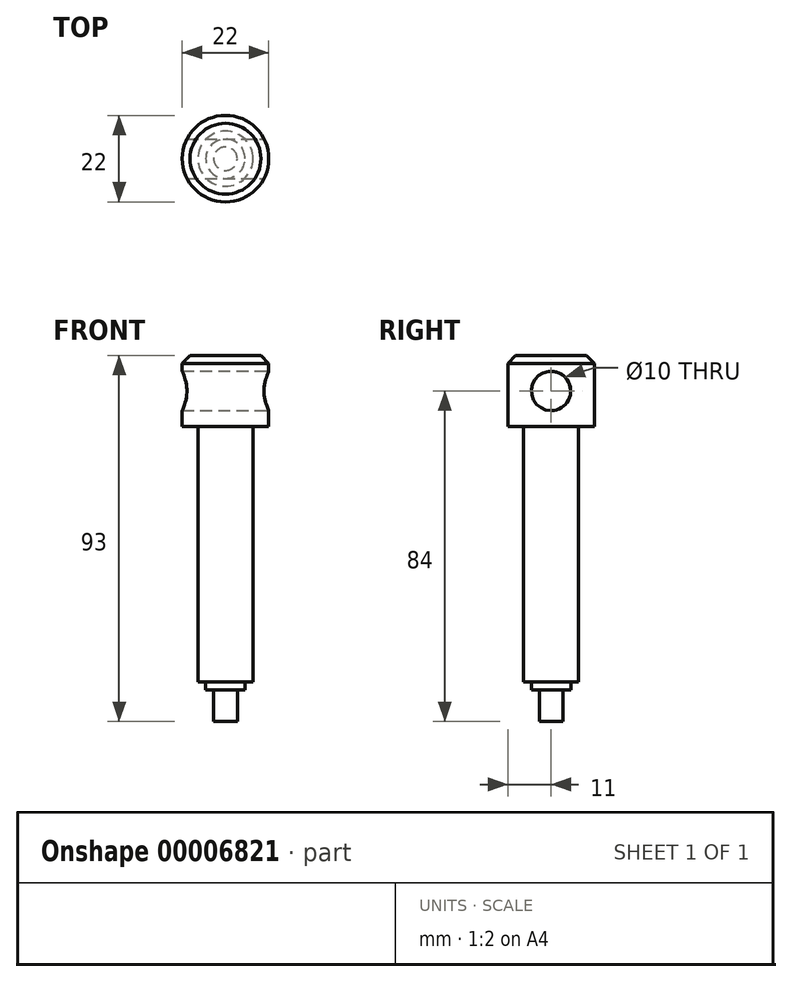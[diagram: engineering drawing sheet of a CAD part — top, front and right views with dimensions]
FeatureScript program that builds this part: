
annotation { "Feature Type Name" : "Feature", "Feature Type Description" : "" }
export const myFeature = defineFeature(function(context is Context, id is Id, definition is map)
    precondition{}
    {
        {
            var Q0;
            Q0=qCreatedBy(makeId("Right.planeOp"),FACE);
            var sketch = newSketch(context, id + "F0", { "sketchPlane" : qUnion([Q0])});
            skLineSegment(sketch, "E0", {"start": v(0, 0) * mm, "end": v(0, -3.09) * mm});
            skLineSegment(sketch, "E1", {"start": v(4.26, -9.53) * mm, "end": v(36, -23) * mm});
            skLineSegment(sketch, "E2", {"start": v(36, -23) * mm, "end": v(70, -23) * mm});
            skLineSegment(sketch, "E3", {"start": v(90, -3) * mm, "end": v(90, 47) * mm});
            skLineSegment(sketch, "E4", {"start": v(70, 67) * mm, "end": v(7, 67) * mm});
            skLineSegment(sketch, "E5", {"start": v(7, 67) * mm, "end": v(7, 45) * mm});
            skLineSegment(sketch, "E6", {"start": v(7, 45) * mm, "end": v(61, 45) * mm});
            skLineSegment(sketch, "E7", {"start": v(68, 38) * mm, "end": v(68, 4) * mm});
            skLineSegment(sketch, "E8", {"start": v(61, -3) * mm, "end": v(36, -3) * mm});
            skLineSegment(sketch, "E9", {"start": v(36, -3) * mm, "end": v(36, 0) * mm});
            skLineSegment(sketch, "E10", {"start": v(36, 0) * mm, "end": v(0, 0) * mm});
            skLineSegment(sketch, "E11", {"start": v(36, -23) * mm, "end": v(21.85, -23) * mm, "construction": true});
            skPoint(sketch, "E12.visualSharp", {"position": v(90, -23) * mm});
            skArc(sketch, "E12.filletArc", {"start": v(70, -23) * mm, "mid": v(84.14, -17.14) * mm, "end": v(90, -3) * mm});
            skPoint(sketch, "E13.visualSharp", {"position": v(90, 67) * mm});
            skArc(sketch, "E13.filletArc", {"start": v(90, 47) * mm, "mid": v(84.14, 61.14) * mm, "end": v(70, 67) * mm});
            skPoint(sketch, "E14.visualSharp", {"position": v(68, 45) * mm});
            skArc(sketch, "E14.filletArc", {"start": v(68, 38) * mm, "mid": v(65.95, 42.95) * mm, "end": v(61, 45) * mm});
            skPoint(sketch, "E15.visualSharp", {"position": v(68, -3) * mm});
            skArc(sketch, "E15.filletArc", {"start": v(61, -3) * mm, "mid": v(65.95, -0.95) * mm, "end": v(68, 4) * mm});
            skPoint(sketch, "E16.visualSharp", {"position": v(0, -7.72) * mm});
            skArc(sketch, "E16.filletArc", {"start": v(0, -3.09) * mm, "mid": v(1.16, -6.95) * mm, "end": v(4.26, -9.53) * mm});
            skSolve(sketch);
        }
        {
            var Q0;
            Q0=qSketchRegion(id+"F0",true);
            extrude(context, id + "F1", {"entities" : qUnion([Q0]), "endBound" : BoundingType.SYMMETRIC, "depth" : 20 * mm});
        }
        {
            var Q0;
            Q0=makeQuery(id+"F1.opExtrude","SWEPT_FACE",FACE,{"disambiguationData":[OSD([sQuery(id+"F0.wireOp",EDGE,"E6")])]});
            var sketch = newSketch(context, id + "F2", { "sketchPlane" : qUnion([Q0])});
            skCircle(sketch, "E17", {"center": v(0, -18) * mm, "radius": 11 * mm});
            skCircle(sketch, "E18", {"center": v(0, -18) * mm, "radius": 7 * mm});
            skSolve(sketch);
        }
        {
            var Q0;
            Q0=qSketchRegion(id+"F2",true);
            extrude(context, id + "F3", {"entities" : qUnion([Q0]), "operationType" : NewBodyOperationType.ADD, "oppositeDirection" : true, "depth" : 25 * mm});
        }
        {
            var Q0;
            Q0=makeQuery(id+"F3.boolean.opBoolean","SPLIT",FACE,{"disambiguationData":[TD([makeQuery(id+"F3.opExtrude","SWEPT_FACE",FACE,{"disambiguationData":[OSD([sQuery(id+"F2.wireOp",EDGE,"E18")])]})])],"derivedFrom":makeQuery(id+"F1.opExtrude","SWEPT_FACE",FACE,{"disambiguationData":[OSD([sQuery(id+"F0.wireOp",EDGE,"E4")])]})});
            var sketch = newSketch(context, id + "F4", { "sketchPlane" : qUnion([Q0])});
            skCircle(sketch, "E19.0", {"center": v(0, 18) * mm, "radius": 7 * mm});
            skSolve(sketch);
        }
        {
            var Q0;
            Q0=qSketchRegion(id+"F4",true);
            extrude(context, id + "F5", {"entities" : qUnion([Q0]), "operationType" : NewBodyOperationType.REMOVE, "oppositeDirection" : true, "depth" : 25 * mm});
        }
        {
            var Q0;
            {var subQ0=sQuery(id+"F0.wireOp",EDGE,"E4");var subQ1=makeQuery(id+"F1.opExtrude","SWEPT_FACE",FACE,{"disambiguationData":[OSD([subQ0])]});var subQ2=sQuery(id+"F0.wireOp",EDGE,"E5");Q0=makeQuery(id+"F3.boolean.opBoolean","SPLIT",FACE,{"disambiguationData":[TD([makeQuery(id+"F1.opExtrude","CAP_FACE",FACE,{"disambiguationData":[OSD([sQuery(id+"F0.wireOp",EDGE,"E0"),sQuery(id+"F0.wireOp",EDGE,"E1"),sQuery(id+"F0.wireOp",EDGE,"E2"),sQuery(id+"F0.wireOp",EDGE,"E3"),subQ0,subQ2,sQuery(id+"F0.wireOp",EDGE,"E6"),sQuery(id+"F0.wireOp",EDGE,"E7"),sQuery(id+"F0.wireOp",EDGE,"E8"),sQuery(id+"F0.wireOp",EDGE,"E9"),sQuery(id+"F0.wireOp",EDGE,"E10"),sQuery(id+"F0.wireOp",EDGE,"E12.filletArc"),sQuery(id+"F0.wireOp",EDGE,"E13.filletArc"),sQuery(id+"F0.wireOp",EDGE,"E14.filletArc"),sQuery(id+"F0.wireOp",EDGE,"E15.filletArc"),sQuery(id+"F0.wireOp",EDGE,"E16.filletArc")])],"isStart":false}),subQ1,makeQuery(id+"F1.opExtrude","SWEPT_FACE",FACE,{"disambiguationData":[OSD([subQ2])]}),makeQuery(id+"F3.opExtrude","SWEPT_FACE",FACE,{"disambiguationData":[OSD([sQuery(id+"F2.wireOp",EDGE,"E17")])]})])],"derivedFrom":subQ1});}
            var sketch = newSketch(context, id + "F6", { "sketchPlane" : qUnion([Q0])});
            skLineSegment(sketch, "E20.1.0", {"start": v(-10, 7) * mm, "end": v(0, 7) * mm});
            skArc(sketch, "E20.1.1", {"start": v(0, 7) * mm, "mid": v(-5.94, 8.74) * mm, "end": v(-10, 13.42) * mm});
            skLineSegment(sketch, "E20.1.2", {"start": v(-10, 13.42) * mm, "end": v(-10, 7) * mm});
            skSolve(sketch);
        }
        {
            var Q0;
            Q0=qSketchRegion(id+"F6",true);
            extrude(context, id + "F7", {"entities" : qUnion([Q0]), "operationType" : NewBodyOperationType.REMOVE, "oppositeDirection" : true, "depth" : 25 * mm});
        }
        {
            var Q0;
            {var subQ0=sQuery(id+"F0.wireOp",EDGE,"E4");var subQ1=makeQuery(id+"F1.opExtrude","SWEPT_FACE",FACE,{"disambiguationData":[OSD([subQ0])]});var subQ2=sQuery(id+"F0.wireOp",EDGE,"E5");Q0=makeQuery(id+"F3.boolean.opBoolean","SPLIT",FACE,{"disambiguationData":[TD([makeQuery(id+"F1.opExtrude","CAP_FACE",FACE,{"disambiguationData":[OSD([sQuery(id+"F0.wireOp",EDGE,"E0"),sQuery(id+"F0.wireOp",EDGE,"E1"),sQuery(id+"F0.wireOp",EDGE,"E2"),sQuery(id+"F0.wireOp",EDGE,"E3"),subQ0,subQ2,sQuery(id+"F0.wireOp",EDGE,"E6"),sQuery(id+"F0.wireOp",EDGE,"E7"),sQuery(id+"F0.wireOp",EDGE,"E8"),sQuery(id+"F0.wireOp",EDGE,"E9"),sQuery(id+"F0.wireOp",EDGE,"E10"),sQuery(id+"F0.wireOp",EDGE,"E12.filletArc"),sQuery(id+"F0.wireOp",EDGE,"E13.filletArc"),sQuery(id+"F0.wireOp",EDGE,"E14.filletArc"),sQuery(id+"F0.wireOp",EDGE,"E15.filletArc"),sQuery(id+"F0.wireOp",EDGE,"E16.filletArc")])],"isStart":false}),subQ1,makeQuery(id+"F1.opExtrude","SWEPT_FACE",FACE,{"disambiguationData":[OSD([subQ2])]}),makeQuery(id+"F3.opExtrude","SWEPT_FACE",FACE,{"disambiguationData":[OSD([sQuery(id+"F2.wireOp",EDGE,"E17")])]})])],"derivedFrom":subQ1});}
            var sketch = newSketch(context, id + "F8", { "sketchPlane" : qUnion([Q0])});
            skArc(sketch, "E21.0", {"start": v(10, 13.42) * mm, "mid": v(5.94, 8.74) * mm, "end": v(0, 7) * mm});
            skLineSegment(sketch, "E22", {"start": v(10, 13.42) * mm, "end": v(10, 7) * mm});
            skLineSegment(sketch, "E23", {"start": v(10, 7) * mm, "end": v(0, 7) * mm});
            skSolve(sketch);
        }
        {
            var Q0;
            Q0=qSketchRegion(id+"F8",true);
            extrude(context, id + "F9", {"entities" : qUnion([Q0]), "operationType" : NewBodyOperationType.REMOVE, "oppositeDirection" : true, "depth" : 25 * mm});
        }
        {
            var Q0;
            Q0=makeQuery(id+"F1.opExtrude","SWEPT_EDGE",EDGE,{"disambiguationData":[OSD([sQuery(id+"F0.wireOp",EDGE,"E8"),sQuery(id+"F0.wireOp",EDGE,"E9")])]});
            fillet(context, id + "F10", {"entities" : qUnion([Q0]), "radius" : 3 * mm, "tangentPropagation" : true, "allowEdgeOverflow" : false});
        }
        {
            var Q0;
            Q0=qCreatedBy(makeId("Right.planeOp"),FACE);
            var sketch = newSketch(context, id + "F11", { "sketchPlane" : qUnion([Q0])});
            skLineSegment(sketch, "E24", {"start": v(11, 100) * mm, "end": v(7, 100) * mm});
            skLineSegment(sketch, "E25", {"start": v(7, 100) * mm, "end": v(7, 118) * mm});
            skLineSegment(sketch, "E26", {"start": v(7, 118) * mm, "end": v(18, 118) * mm});
            skLineSegment(sketch, "E27", {"start": v(18, 118) * mm, "end": v(18, 35) * mm});
            skLineSegment(sketch, "E28", {"start": v(11, 100) * mm, "end": v(11, 35) * mm});
            skLineSegment(sketch, "E29", {"start": v(11, 35) * mm, "end": v(18, 35) * mm});
            skSolve(sketch);
        }
        {
            var Q0;
            Q0=qSketchRegion(id+"F11",true);
            var Q1;
            Q1=sQuery(id+"F11.wireOp",EDGE,"E27");
            revolve(context, id + "F12", {"entities" : qUnion([Q0]), "axis" : qUnion([Q1]), "revolveType" : RevolveType.FULL});
        }
        {
            var Q0;
            Q0=makeQuery(id+"F12.opRevolve","SWEPT_EDGE",EDGE,{"disambiguationData":[OSD([sQuery(id+"F11.wireOp",EDGE,"E25"),sQuery(id+"F11.wireOp",EDGE,"E26")])]});
            chamfer(context, id + "F13", {"entities" : qUnion([Q0]), "width" : 2 * mm, "tangentPropagation" : true});
        }
        {
            var Q0;
            Q0=makeQuery(id+"F12.opRevolve","SWEPT_FACE",FACE,{"disambiguationData":[OSD([sQuery(id+"F11.wireOp",EDGE,"E29")])]});
            var sketch = newSketch(context, id + "F14", { "sketchPlane" : qUnion([Q0])});
            skCircle(sketch, "E30", {"center": v(0, -18) * mm, "radius": 5 * mm});
            skSolve(sketch);
        }
        {
            var Q0;
            Q0=qSketchRegion(id+"F14",true);
            extrude(context, id + "F15", {"entities" : qUnion([Q0]), "operationType" : NewBodyOperationType.ADD, "depth" : 2 * mm});
        }
        {
            var Q0;
            Q0=makeQuery(id+"F15.opExtrude","CAP_FACE",FACE,{"disambiguationData":[OSD([sQuery(id+"F14.wireOp",EDGE,"E30")])],"isStart":false});
            var sketch = newSketch(context, id + "F16", { "sketchPlane" : qUnion([Q0])});
            skCircle(sketch, "E31", {"center": v(0, -18) * mm, "radius": 3 * mm});
            skSolve(sketch);
        }
        {
            var Q0;
            Q0=qSketchRegion(id+"F16",true);
            extrude(context, id + "F17", {"entities" : qUnion([Q0]), "operationType" : NewBodyOperationType.ADD, "depth" : 8 * mm});
        }
        {
            var Q0;
            Q0=qCreatedBy(makeId("Right.planeOp"),FACE);
            var sketch = newSketch(context, id + "F18", { "sketchPlane" : qUnion([Q0])});
            skCircle(sketch, "E32", {"center": v(18, 109) * mm, "radius": 5 * mm});
            skSolve(sketch);
        }
        {
            var Q0;
            Q0=qSketchRegion(id+"F18",true);
            extrude(context, id + "F19", {"entities" : qUnion([Q0]), "operationType" : NewBodyOperationType.REMOVE, "oppositeDirection" : true, "depth" : 25 * mm});
        }
        {
            var Q0;
            Q0=makeQuery(id+"F19.boolean.opBoolean","COPY",FACE,{"derivedFrom":makeQuery(id+"F19.opExtrude","CAP_FACE",FACE,{"disambiguationData":[OSD([sQuery(id+"F18.wireOp",EDGE,"E32")])],"isStart":true})});
            var sketch = newSketch(context, id + "F20", { "sketchPlane" : qUnion([Q0])});
            skCircle(sketch, "E33.0", {"center": v(-18, 109) * mm, "radius": 5 * mm});
            skSolve(sketch);
        }
        {
            var Q0;
            Q0=qSketchRegion(id+"F20",true);
            extrude(context, id + "F21", {"entities" : qUnion([Q0]), "operationType" : NewBodyOperationType.REMOVE, "oppositeDirection" : true, "depth" : 25 * mm});
        }
        {
            var Q0;
            Q0=qCreatedBy(makeId("Right.planeOp"),FACE);
            var sketch = newSketch(context, id + "F22", { "sketchPlane" : qUnion([Q0])});
            skCircle(sketch, "E34.0", {"center": v(18, 109) * mm, "radius": 5 * mm});
            skSolve(sketch);
        }
        {
            var Q0;
            Q0=qSketchRegion(id+"F22",true);
            extrude(context, id + "F23", {"entities" : qUnion([Q0]), "endBound" : BoundingType.SYMMETRIC, "depth" : 89 * mm});
        }
        {
            var Q0;
            Q0=makeQuery(id+"F23.opExtrude","CAP_FACE",FACE,{"disambiguationData":[OSD([sQuery(id+"F22.wireOp",EDGE,"E34.0")])],"isStart":false});
            var sketch = newSketch(context, id + "F24", { "sketchPlane" : qUnion([Q0])});
            skCircle(sketch, "E35", {"center": v(18, 109) * mm, "radius": 3 * mm});
            skSolve(sketch);
        }
        {
            var Q0;
            Q0=qSketchRegion(id+"F24",true);
            extrude(context, id + "F25", {"entities" : qUnion([Q0]), "operationType" : NewBodyOperationType.ADD, "depth" : 12 * mm});
        }
        {
            var Q0;
            Q0=makeQuery(id+"F23.opExtrude","CAP_FACE",FACE,{"disambiguationData":[OSD([sQuery(id+"F22.wireOp",EDGE,"E34.0")])],"isStart":true});
            var sketch = newSketch(context, id + "F26", { "sketchPlane" : qUnion([Q0])});
            skCircle(sketch, "E36", {"center": v(-18, 109) * mm, "radius": 3 * mm});
            skSolve(sketch);
        }
        {
            var Q0;
            Q0=qSketchRegion(id+"F26",true);
            extrude(context, id + "F27", {"entities" : qUnion([Q0]), "operationType" : NewBodyOperationType.ADD, "depth" : 12 * mm});
        }
        {
            var Q0;
            Q0=makeQuery(id+"F25.opExtrude","CAP_FACE",FACE,{"disambiguationData":[OSD([sQuery(id+"F24.wireOp",EDGE,"E35")])],"isStart":false});
            var sketch = newSketch(context, id + "F28", { "sketchPlane" : qUnion([Q0])});
            skCircle(sketch, "E37.0", {"center": v(18, 109) * mm, "radius": 3 * mm});
            skCircle(sketch, "E38", {"center": v(18, 109) * mm, "radius": 10 * mm});
            skSolve(sketch);
        }
        {
            var Q0;
            Q0=qSketchRegion(id+"F28",true);
            extrude(context, id + "F29", {"entities" : qUnion([Q0]), "oppositeDirection" : true, "depth" : 10 * mm});
        }
        {
            var Q0;
            Q0=makeQuery(id+"F29.opExtrude","CAP_EDGE",EDGE,{"disambiguationData":[OSD([sQuery(id+"F28.wireOp",EDGE,"E38")])],"isStart":true});
            var Q1;
            Q1=makeQuery(id+"F29.opExtrude","CAP_EDGE",EDGE,{"disambiguationData":[OSD([sQuery(id+"F28.wireOp",EDGE,"E38")])],"isStart":false});
            chamfer(context, id + "F30", {"entities" : qUnion([Q0, Q1]), "width" : 2 * mm, "tangentPropagation" : true});
        }
        {
            var Q0;
            Q0=makeQuery(id+"F29.opExtrude","SWEPT_BODY",BODY,{"disambiguationData":[OSD([sQuery(id+"F28.wireOp",EDGE,"E37.0"),sQuery(id+"F28.wireOp",EDGE,"E38")])]});
            var Q1;
            Q1=qCreatedBy(makeId("Right.planeOp"),FACE);
            mirror(context, id + "F31", {"entities" : qUnion([Q0]), "mirrorPlane" : qUnion([Q1])});
        }
        {
            var Q0;
            Q0=qCreatedBy(makeId("Right.planeOp"),FACE);
            var sketch = newSketch(context, id + "F32", { "sketchPlane" : qUnion([Q0])});
            skLineSegment(sketch, "E39", {"start": v(21, 30) * mm, "end": v(21, 32) * mm});
            skLineSegment(sketch, "E40", {"start": v(34.36, 22) * mm, "end": v(36.5, 22) * mm});
            skArc(sketch, "E41", {"start": v(36.5, 22) * mm, "mid": v(30.47, 29.67) * mm, "end": v(21, 32) * mm});
            skArc(sketch, "E42.0", {"start": v(34.36, 22) * mm, "mid": v(29, 28.23) * mm, "end": v(21, 30) * mm});
            skLineSegment(sketch, "E43", {"start": v(18, 24.98) * mm, "end": v(18, 32) * mm});
            skSolve(sketch);
        }
        {
            var Q0;
            Q0=qSketchRegion(id+"F32",true);
            var Q1;
            Q1=sQuery(id+"F32.wireOp",EDGE,"E43");
            revolve(context, id + "F33", {"entities" : qUnion([Q0]), "axis" : qUnion([Q1]), "revolveType" : RevolveType.FULL});
        }
        {
            var Q0;
            Q0=makeQuery(id+"F1.opExtrude","SWEPT_BODY",BODY,{"disambiguationData":[OSD([sQuery(id+"F0.wireOp",EDGE,"E0"),sQuery(id+"F0.wireOp",EDGE,"E1"),sQuery(id+"F0.wireOp",EDGE,"E2"),sQuery(id+"F0.wireOp",EDGE,"E3"),sQuery(id+"F0.wireOp",EDGE,"E4"),sQuery(id+"F0.wireOp",EDGE,"E5"),sQuery(id+"F0.wireOp",EDGE,"E6"),sQuery(id+"F0.wireOp",EDGE,"E7"),sQuery(id+"F0.wireOp",EDGE,"E8"),sQuery(id+"F0.wireOp",EDGE,"E9"),sQuery(id+"F0.wireOp",EDGE,"E10"),sQuery(id+"F0.wireOp",EDGE,"E12.filletArc"),sQuery(id+"F0.wireOp",EDGE,"E13.filletArc"),sQuery(id+"F0.wireOp",EDGE,"E14.filletArc"),sQuery(id+"F0.wireOp",EDGE,"E15.filletArc"),sQuery(id+"F0.wireOp",EDGE,"E16.filletArc")])]});
            deleteBodies(context, id + "F34", {"entities" : qUnion([Q0])});
        }
        {
            var Q0;
            Q0=makeQuery(id+"F23.opExtrude","SWEPT_BODY",BODY,{"disambiguationData":[OSD([sQuery(id+"F22.wireOp",EDGE,"E34.0")])]});
            deleteBodies(context, id + "F35", {"entities" : qUnion([Q0])});
        }
        {
            var Q0;
            Q0=makeQuery(id+"F31.opPattern","COPY",BODY,{"derivedFrom":makeQuery(id+"F29.opExtrude","SWEPT_BODY",BODY,{"disambiguationData":[OSD([sQuery(id+"F28.wireOp",EDGE,"E37.0"),sQuery(id+"F28.wireOp",EDGE,"E38")])]}),"instanceName":"1"});
            deleteBodies(context, id + "F36", {"entities" : qUnion([Q0])});
        }
        {
            var Q0;
            Q0=makeQuery(id+"F29.opExtrude","SWEPT_BODY",BODY,{"disambiguationData":[OSD([sQuery(id+"F28.wireOp",EDGE,"E37.0"),sQuery(id+"F28.wireOp",EDGE,"E38")])]});
            deleteBodies(context, id + "F37", {"entities" : qUnion([Q0])});
        }
        {
            var Q0;
            Q0=makeQuery(id+"F33.opRevolve","SWEPT_BODY",BODY,{"disambiguationData":[OSD([sQuery(id+"F32.wireOp",EDGE,"E39"),sQuery(id+"F32.wireOp",EDGE,"E40"),sQuery(id+"F32.wireOp",EDGE,"E41"),sQuery(id+"F32.wireOp",EDGE,"E42.0")])]});
            deleteBodies(context, id + "F38", {"entities" : qUnion([Q0])});
        }
    });
